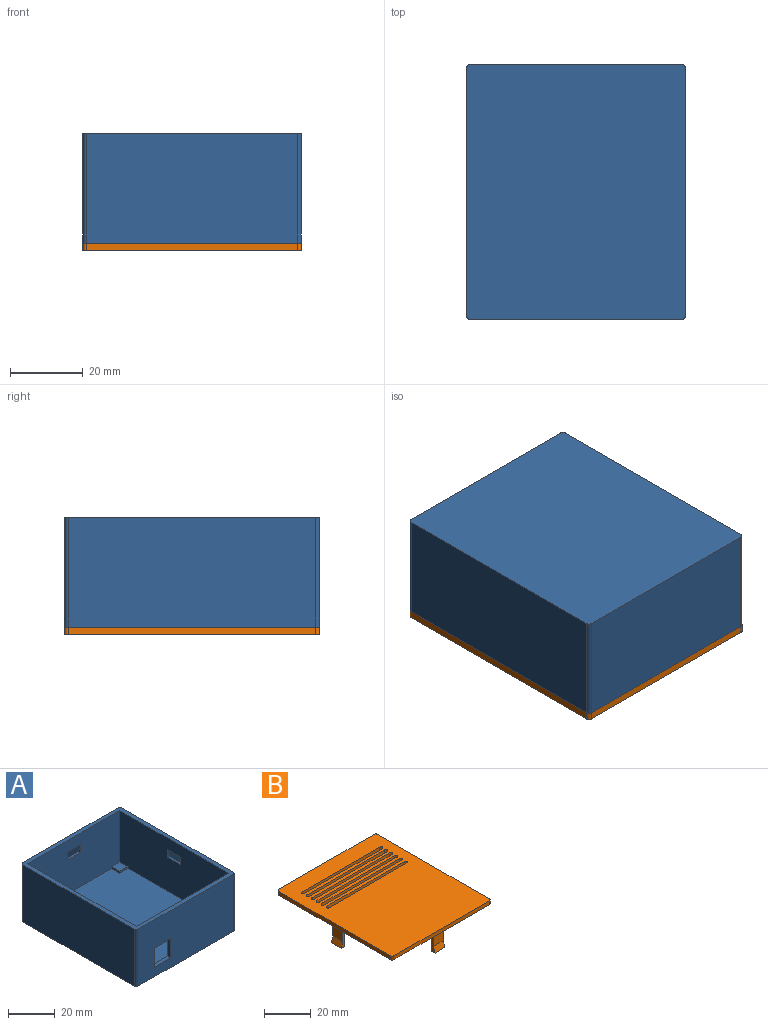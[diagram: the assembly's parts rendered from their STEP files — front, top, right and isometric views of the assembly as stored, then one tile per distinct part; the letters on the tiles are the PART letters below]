
ASSEMBLY  parts=2 mates=1
PART A: 52 faces, bbox 60x70x30 mm
  f0: plane 68x30mm, normal (1,0,0), area 1940mm2, adj f11,f14,f29,f30,f47,f48,f49,f50
  f1: plane 56x28mm, normal (0,1,0), area 1426mm2, adj f3,f6,f10,f11,f19,f20,f22,f23
  f2: plane 58x30mm, normal (0,-1,0), area 1640mm2, adj f11,f14,f28,f29,f43,f44,f45,f46
  f3: plane 66x28mm, normal (-1,0,0), area 1806mm2, adj f1,f9,f10,f11,f15,f17,f18,f20
  f4: plane 4x1mm, normal (0,1,0), area 2mm2, adj f6,f37,f38
  f5: plane 4x1mm, normal (0,-1,0), area 2mm2, adj f6,f37,f38
  f6: plane 66x28mm, normal (1,0,0), area 1806mm2, adj f1,f4,f5,f9,f10,f11,f21,f23
  f7: plane 4x1mm, normal (1,0,0), area 2mm2, adj f9,f31,f32
  f8: plane 4x1mm, normal (-1,0,0), area 2mm2, adj f9,f31,f32
  f9: plane 56x28mm, normal (0,-1,0), area 1526mm2, adj f3,f6,f7,f8,f10,f11,f16,f17
  f10: plane 66x56mm, normal (0,0,1), area 3596mm2, adj f1,f3,f6,f9,f15,f16,f18,f19
  f11: plane 70x60mm, normal (0,0,1), area 503.1mm2, adj f0,f1,f2,f3,f6,f9,f12,f13
  f12: plane 58x30mm, normal (0,1,0), area 1740mm2, adj f11,f14,f27,f30
  f13: plane 68x30mm, normal (-1,0,0), area 2040mm2, adj f11,f14,f27,f28
  f14: plane 70x60mm, normal (0,0,-1), area 4199.1mm2, adj f0,f2,f12,f13,f27,f28,f29,f30
  f15: plane 5x1mm, normal (0,-1,0), area 5mm2, adj f3,f10,f16,f17
  f16: plane 5x1mm, normal (-1,0,0), area 5mm2, adj f9,f10,f15,f17
  f17: plane 5x5mm, normal (0,0,1), area 25mm2, adj f3,f9,f15,f16
  f18: plane 5x1mm, normal (0,1,0), area 5mm2, adj f3,f10,f19,f20
  f19: plane 5x1mm, normal (-1,0,0), area 5mm2, adj f1,f10,f18,f20
  f20: plane 5x5mm, normal (0,0,1), area 25mm2, adj f1,f3,f18,f19
  f21: plane 5x1mm, normal (0,1,0), area 5mm2, adj f6,f10,f22,f23
  f22: plane 5x1mm, normal (1,0,0), area 5mm2, adj f1,f10,f21,f23
  f23: plane 5x5mm, normal (0,0,1), area 25mm2, adj f1,f6,f21,f22
  f24: plane 5x1mm, normal (0,-1,0), area 5mm2, adj f6,f10,f25,f26
  f25: plane 5x1mm, normal (1,0,0), area 5mm2, adj f9,f10,f24,f26
  f26: plane 5x5mm, normal (0,0,1), area 25mm2, adj f6,f9,f24,f25
  f27: cylinder r=1mm len=30mm, axis (0,0,1), area 47.1mm2, adj f11,f12,f13,f14
  f28: cylinder r=1mm len=30mm, axis (0,0,-1), area 47.1mm2, adj f2,f11,f13,f14
  f29: cylinder r=1mm len=30mm, axis (0,0,1), area 47.1mm2, adj f0,f2,f11,f14
  f30: cylinder r=1mm len=30mm, axis (0,0,-1), area 47.1mm2, adj f0,f11,f12,f14
  f31: plane 8x1mm, normal (0,0,1), area 8mm2, adj f7,f8,f9,f32
  f32: plane 8x4mm, normal (0,-0.97,-0.24), area 33mm2, adj f7,f8,f9,f31
  f33: plane 4x1mm, normal (-1,0,0), area 2mm2, adj f1,f34,f36
  f34: plane 8x1mm, normal (0,0,1), area 8mm2, adj f1,f33,f35,f36
  f35: plane 4x1mm, normal (1,0,0), area 2mm2, adj f1,f34,f36
  f36: plane 8x4mm, normal (0,0.97,-0.24), area 33mm2, adj f1,f33,f34,f35
  f37: plane 8x1mm, normal (0,0,1), area 8mm2, adj f4,f5,f6,f38
  f38: plane 8x4mm, normal (0.97,0,-0.24), area 33mm2, adj f4,f5,f6,f37
  f39: plane 4x1mm, normal (0,-1,0), area 2mm2, adj f3,f40,f42
  f40: plane 8x1mm, normal (0,0,1), area 8mm2, adj f3,f39,f41,f42
  f41: plane 4x1mm, normal (0,1,0), area 2mm2, adj f3,f40,f42
  f42: plane 8x4mm, normal (-0.97,0,-0.24), area 33mm2, adj f3,f39,f40,f41
  f43: plane 10x2mm, normal (0,0,-1), area 20mm2, adj f1,f2,f44,f46
  f44: plane 10x2mm, normal (1,0,0), area 20mm2, adj f1,f2,f43,f45
  f45: plane 10x2mm, normal (0,0,1), area 20mm2, adj f1,f2,f44,f46
  f46: plane 10x2mm, normal (-1,0,0), area 20mm2, adj f1,f2,f43,f45
  f47: plane 10x1.4mm, normal (0,0,-1), area 14mm2, adj f0,f48,f50,f51
  f48: plane 10x1.4mm, normal (0,1,0), area 14mm2, adj f0,f47,f49,f51
  f49: plane 10x1.4mm, normal (0,0,1), area 14mm2, adj f0,f48,f50,f51
  f50: plane 10x1.4mm, normal (0,-1,0), area 14mm2, adj f0,f47,f49,f51
  f51: plane 10x10mm, normal (1,0,0), area 100mm2, adj f47,f48,f49,f50
PART B: 70 faces, bbox 60x70x12 mm
  f0: plane 10x2mm, normal (0,1,0), area 11.5mm2, adj f1,f11,f60,f61,f69
  f1: plane 7x6mm, normal (-1,0,0), area 42mm2, adj f0,f11,f59,f69
  f2: plane 10x2mm, normal (1,0,0), area 11.5mm2, adj f4,f11,f64,f65,f68
  f3: plane 10x2mm, normal (-1,0,0), area 11.5mm2, adj f4,f11,f64,f65,f68
  f4: plane 7x6mm, normal (0,1,0), area 42mm2, adj f2,f3,f11,f68
  f5: plane 10x2mm, normal (0,-1,0), area 11.5mm2, adj f7,f11,f62,f63,f67
  f6: plane 10x2mm, normal (0,1,0), area 11.5mm2, adj f7,f11,f62,f63,f67
  f7: plane 7x6mm, normal (1,0,0), area 42mm2, adj f5,f6,f11,f67
  f8: plane 10x2mm, normal (-1,0,0), area 11.5mm2, adj f10,f11,f57,f58,f66
  f9: plane 10x2mm, normal (1,0,0), area 11.5mm2, adj f10,f11,f57,f58,f66
  f10: plane 7x6mm, normal (0,-1,0), area 42mm2, adj f8,f9,f11,f66
  f11: plane 70x60mm, normal (0,0,-1), area 3730.9mm2, adj f0,f1,f2,f3,f4,f5,f6,f7
  f12: plane 70x60mm, normal (0,0,1), area 3754.9mm2, adj f13,f14,f15,f16,f17,f18,f19,f20
  f13: plane 58x2mm, normal (0,1,0), area 116mm2, adj f11,f12,f17,f20
  f14: plane 68x2mm, normal (-1,0,0), area 136mm2, adj f11,f12,f17,f18
  f15: plane 58x2mm, normal (0,-1,0), area 116mm2, adj f11,f12,f18,f19
  f16: plane 68x2mm, normal (1,0,0), area 136mm2, adj f11,f12,f19,f20
  f17: cylinder r=1mm len=2mm, axis (0,0,-1), area 3.1mm2, adj f11,f12,f13,f14
  f18: cylinder r=1mm len=2mm, axis (0,0,1), area 3.1mm2, adj f11,f12,f14,f15
  f19: cylinder r=1mm len=2mm, axis (0,0,-1), area 3.1mm2, adj f11,f12,f15,f16
  f20: cylinder r=1mm len=2mm, axis (0,0,1), area 3.1mm2, adj f11,f12,f13,f16
  f21: plane 47.08x2mm, normal (0,-1,0), area 94.2mm2, adj f11,f12,f54,f55
  f22: plane 47.08x2mm, normal (0,1,0), area 94.2mm2, adj f11,f12,f53,f56
  f23: plane 47.08x2mm, normal (0,-1,0), area 94.2mm2, adj f11,f12,f34,f35
  f24: plane 47.08x2mm, normal (0,1,0), area 94.2mm2, adj f11,f12,f33,f36
  f25: plane 47.08x2mm, normal (0,-1,0), area 94.2mm2, adj f11,f12,f38,f39
  f26: plane 47.08x2mm, normal (0,1,0), area 94.2mm2, adj f11,f12,f37,f40
  f27: plane 47.08x2mm, normal (0,-1,0), area 94.2mm2, adj f11,f12,f42,f43
  f28: plane 47.08x2mm, normal (0,1,0), area 94.2mm2, adj f11,f12,f41,f44
  f29: plane 47.08x2mm, normal (0,-1,0), area 94.2mm2, adj f11,f12,f46,f47
  f30: plane 47.08x2mm, normal (0,1,0), area 94.2mm2, adj f11,f12,f45,f48
  f31: plane 47.08x2mm, normal (0,-1,0), area 94.2mm2, adj f11,f12,f50,f51
  f32: plane 47.08x2mm, normal (0,1,0), area 94.2mm2, adj f11,f12,f49,f52
  f33: cylinder r=1mm len=2mm, axis (0,0,-1), area 2.7mm2, adj f11,f12,f24,f34
  f34: cylinder r=1mm len=2mm, axis (0,0,1), area 2.7mm2, adj f11,f12,f23,f33
  f35: cylinder r=1mm len=2mm, axis (0,0,-1), area 2.7mm2, adj f11,f12,f23,f36
  f36: cylinder r=1mm len=2mm, axis (0,0,1), area 2.7mm2, adj f11,f12,f24,f35
  f37: cylinder r=1mm len=2mm, axis (0,0,-1), area 2.7mm2, adj f11,f12,f26,f38
  f38: cylinder r=1mm len=2mm, axis (0,0,1), area 2.7mm2, adj f11,f12,f25,f37
  f39: cylinder r=1mm len=2mm, axis (0,0,-1), area 2.7mm2, adj f11,f12,f25,f40
  f40: cylinder r=1mm len=2mm, axis (0,0,1), area 2.7mm2, adj f11,f12,f26,f39
  f41: cylinder r=1mm len=2mm, axis (0,0,-1), area 2.7mm2, adj f11,f12,f28,f42
  f42: cylinder r=1mm len=2mm, axis (0,0,1), area 2.7mm2, adj f11,f12,f27,f41
  f43: cylinder r=1mm len=2mm, axis (0,0,-1), area 2.7mm2, adj f11,f12,f27,f44
  f44: cylinder r=1mm len=2mm, axis (0,0,1), area 2.7mm2, adj f11,f12,f28,f43
  f45: cylinder r=1mm len=2mm, axis (0,0,-1), area 2.7mm2, adj f11,f12,f30,f46
  f46: cylinder r=1mm len=2mm, axis (0,0,1), area 2.7mm2, adj f11,f12,f29,f45
  f47: cylinder r=1mm len=2mm, axis (0,0,-1), area 2.7mm2, adj f11,f12,f29,f48
  f48: cylinder r=1mm len=2mm, axis (0,0,1), area 2.7mm2, adj f11,f12,f30,f47
  f49: cylinder r=1mm len=2mm, axis (0,0,-1), area 2.7mm2, adj f11,f12,f32,f50
  f50: cylinder r=1mm len=2mm, axis (0,0,1), area 2.7mm2, adj f11,f12,f31,f49
  f51: cylinder r=1mm len=2mm, axis (0,0,-1), area 2.7mm2, adj f11,f12,f31,f52
  f52: cylinder r=1mm len=2mm, axis (0,0,1), area 2.7mm2, adj f11,f12,f32,f51
  f53: cylinder r=1mm len=2mm, axis (0,0,-1), area 2.7mm2, adj f11,f12,f22,f54
  f54: cylinder r=1mm len=2mm, axis (0,0,1), area 2.7mm2, adj f11,f12,f21,f53
  f55: cylinder r=1mm len=2mm, axis (0,0,-1), area 2.7mm2, adj f11,f12,f21,f56
  f56: cylinder r=1mm len=2mm, axis (0,0,1), area 2.7mm2, adj f11,f12,f22,f55
  f57: plane 10x6mm, normal (0,1,0), area 60mm2, adj f8,f9,f11,f58
  f58: plane 6x2mm, normal (0,0,-1), area 12mm2, adj f8,f9,f57,f66
  f59: plane 10x2mm, normal (0,-1,0), area 11.5mm2, adj f1,f11,f60,f61,f69
  f60: plane 10x6mm, normal (1,0,0), area 60mm2, adj f0,f11,f59,f61
  f61: plane 6x2mm, normal (0,0,-1), area 12mm2, adj f0,f59,f60,f69
  f62: plane 10x6mm, normal (-1,0,0), area 60mm2, adj f5,f6,f11,f63
  f63: plane 6x2mm, normal (0,0,-1), area 12mm2, adj f5,f6,f62,f67
  f64: plane 10x6mm, normal (0,-1,0), area 60mm2, adj f2,f3,f11,f65
  f65: plane 6x2mm, normal (0,0,-1), area 12mm2, adj f2,f3,f64,f68
  f66: plane 6x3mm, normal (0,-0.95,0.32), area 19mm2, adj f8,f9,f10,f58
  f67: plane 6x3mm, normal (0.95,0,0.32), area 19mm2, adj f5,f6,f7,f63
  f68: plane 6x3mm, normal (0,0.95,0.32), area 19mm2, adj f2,f3,f4,f65
  f69: plane 6x3mm, normal (-0.95,0,0.32), area 19mm2, adj f0,f1,f59,f61
PLACE A rot(axis=(1,0,0),180deg) t=(-11.58,93.13,63.27)mm
PLACE B rot(axis=(1,0,0),180deg) t=(-25,94.91,31.27)mm
MATE fastened B.f11 <-> A.f11  axis (0,0,1) through (-49.9,45.18,33.27)mm
